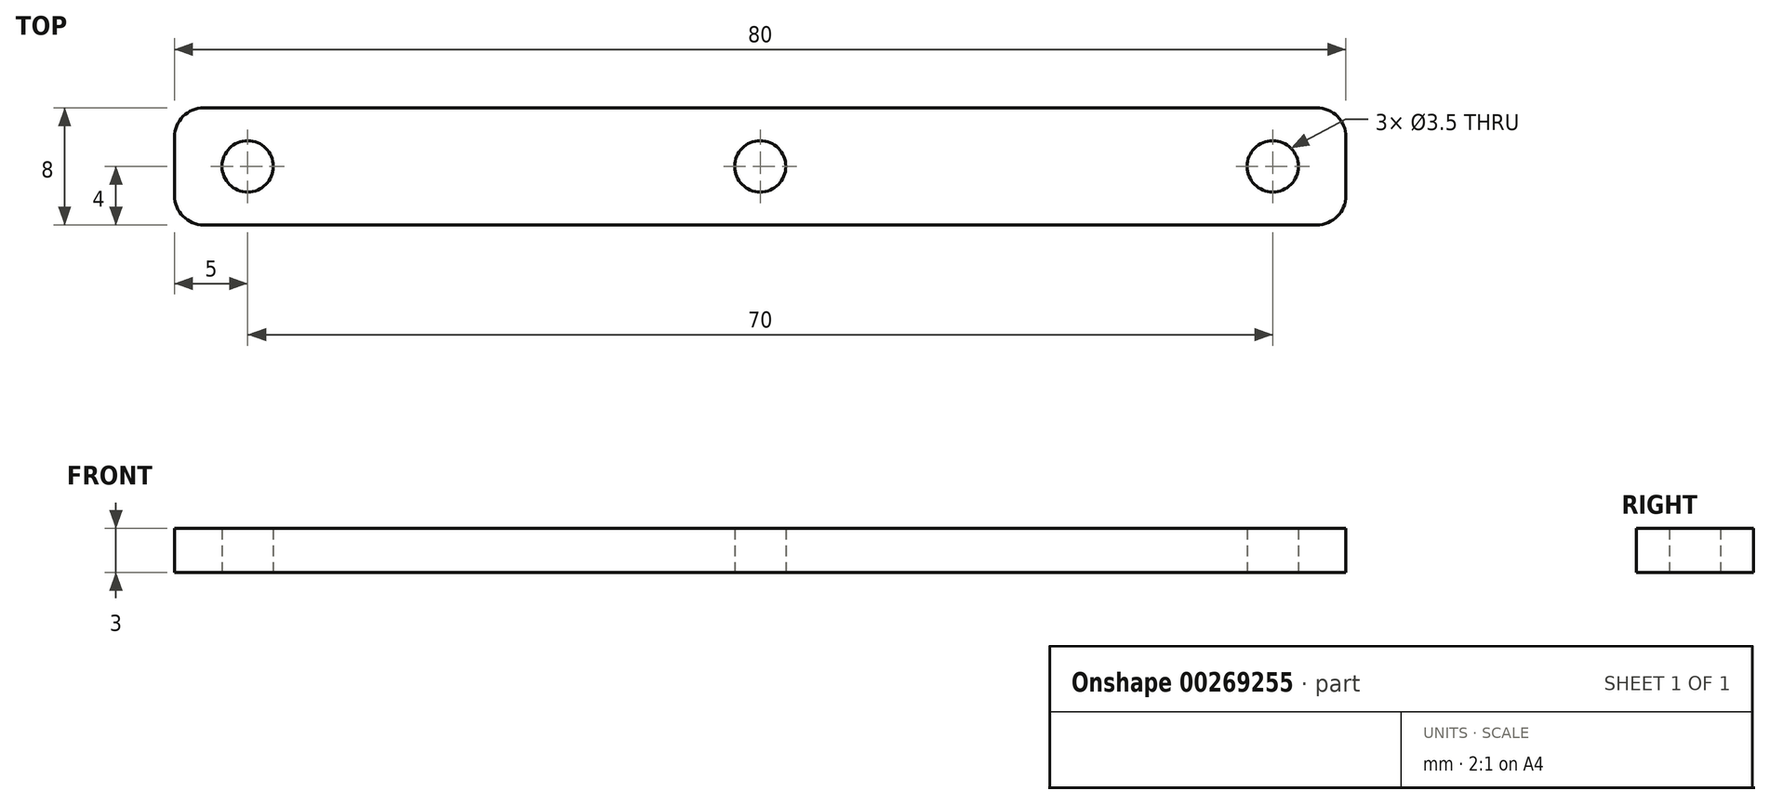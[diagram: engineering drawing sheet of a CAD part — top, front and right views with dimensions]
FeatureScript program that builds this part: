
annotation { "Feature Type Name" : "Feature", "Feature Type Description" : "" }
export const myFeature = defineFeature(function(context is Context, id is Id, definition is map)
    precondition{}
    {
        {
            var Q0;
            Q0=qCreatedBy(makeId("Top.planeOp"),FACE);
            var sketch = newSketch(context, id + "F0", { "sketchPlane" : qUnion([Q0])});
            skLineSegment(sketch, "E0.bottom", {"start": v(40, -4) * mm, "end": v(-40, -4) * mm});
            skLineSegment(sketch, "E0.top", {"start": v(40, 4) * mm, "end": v(-40, 4) * mm});
            skLineSegment(sketch, "E0.left", {"start": v(40, -4) * mm, "end": v(40, 4) * mm});
            skLineSegment(sketch, "E0.right", {"start": v(-40, -4) * mm, "end": v(-40, 4) * mm});
            skPoint(sketch, "E0.middle", {"position": v(0, 0) * mm});
            skCircle(sketch, "E1", {"center": v(0, 0) * mm, "radius": 1.75 * mm});
            skCircle(sketch, "E2", {"center": v(-35, 0) * mm, "radius": 1.75 * mm});
            skCircle(sketch, "E3", {"center": v(35, 0) * mm, "radius": 1.75 * mm});
            skSolve(sketch);
        }
        {
            var Q0;
            Q0 = qSketchRegion(id + "F0", true);
            extrude(context, id + "F1", {"entities" : qUnion([Q0]), "depth" : 3 * mm});
        }
        {
            var Q0;
            Q0=makeQuery(id+"F1.opExtrude","SWEPT_EDGE",EDGE,{"disambiguationData":[OSD([sQuery(id+"F0.wireOp",EDGE,"E0.bottom"),sQuery(id+"F0.wireOp",EDGE,"E0.right")])]});
            var Q1;
            Q1=makeQuery(id+"F1.opExtrude","SWEPT_EDGE",EDGE,{"disambiguationData":[OSD([sQuery(id+"F0.wireOp",EDGE,"E0.bottom"),sQuery(id+"F0.wireOp",EDGE,"E0.left")])]});
            var Q2;
            Q2=makeQuery(id+"F1.opExtrude","SWEPT_EDGE",EDGE,{"disambiguationData":[OSD([sQuery(id+"F0.wireOp",EDGE,"E0.top"),sQuery(id+"F0.wireOp",EDGE,"E0.left")])]});
            var Q3;
            Q3=makeQuery(id+"F1.opExtrude","SWEPT_EDGE",EDGE,{"disambiguationData":[OSD([sQuery(id+"F0.wireOp",EDGE,"E0.top"),sQuery(id+"F0.wireOp",EDGE,"E0.right")])]});
            fillet(context, id + "F2", {"entities" : qUnion([Q0, Q1, Q2, Q3]), "radius" : 2 * mm, "tangentPropagation" : true, "allowEdgeOverflow" : false});
        }
    });
